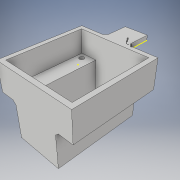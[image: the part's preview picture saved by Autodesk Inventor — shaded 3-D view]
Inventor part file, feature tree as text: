
AUTODESK INVENTOR PART (.ipt)
format: ipt  version: 2019 (Build 230136000, 136)  size: 242,688 bytes
history: native  units: mm
features: sketch x8, projected_geometry x8, extrude x7, chamfer x3
ambient origin geometry x8: Origin, YZ Plane, XZ Plane, XY Plane, X Axis, Y Axis, Z Axis, Center Point
bodies: Solid1 (feature_tree)
feature tree (26):
  extrude  "Extrusion1"  Depth=16.1mm
  extrude  "Extrusion2"  Depth=29.0mm
  extrude  "Extrusion3"  Depth=54.0mm
  extrude  "Extrusion4"  Depth=14.25mm
  extrude  "Extrusion5"  Depth=3.0mm TaperAngle=0.0deg
  chamfer  "Chamfer1"  Distance=25.0mm
  chamfer  "Chamfer2"  Distance=3.0mm
  extrude  "Extrusion6"  Depth=45.0mm
  extrude  "Extrusion7"  Depth=48.0mm
  chamfer  "Chamfer3"  Distance=15.0mm
  sketch  "Sketch8"  dims[d15=51.0mm d16=3.0mm d17=0.0mm d18=45.0mm d19=48.0mm d20=15.0mm d21=0.0mm d22=3.5mm d23=4.0mm d24=4.0mm d25=4.0mm d26=20.0mm d28=40.0mm d29=20.0mm d31=37.0mm d34=10.0mm d35=0.0mm d36=2.0mm d37=2.0mm d38=45.0deg d39=2.0mm d40=2.0mm d41=45.0deg d42=6.0mm d43=20.0mm d45=40.0mm d46=20.0mm d48=37.0mm d51=10.0mm d52=0.0mm d53=4.0mm d54=15.0mm d55=3.0mm d56=18.0mm d57=18.0mm d58=16.0mm d59=0.0mm d60=2.0mm d61=2.0mm d62=45.0deg d63=6.0mm]
  sketch  "Sketch1"  dims[d0=16.1mm d1=16.1mm]
  sketch  "Sketch2"  dims[d2=25.5mm d3=29.0mm]
  sketch  "Sketch3"  dims[d4=54.0mm d5=14.5mm]
  sketch  "Sketch4"  dims[d6=14.5mm d7=14.25mm]
  sketch  "Sketch5"  dims[d8=14.25mm d9=3.0mm d10=0.0mm]
  projected_geometry  "Projected Loop1"
  projected_geometry  "Projected Loop2"
  projected_geometry  "Projected Loop3"
  projected_geometry  "Projected Loop4"
  sketch  "Sketch6"  dims[d11=23.0mm]
  projected_geometry  "Projected Loop5"
  projected_geometry  "Projected Loop6"
  sketch  "Sketch7"  dims[d12=48.0mm d13=25.0mm d14=0.0mm]
  projected_geometry  "Projected Loop7"
  projected_geometry  "Projected Loop8"
